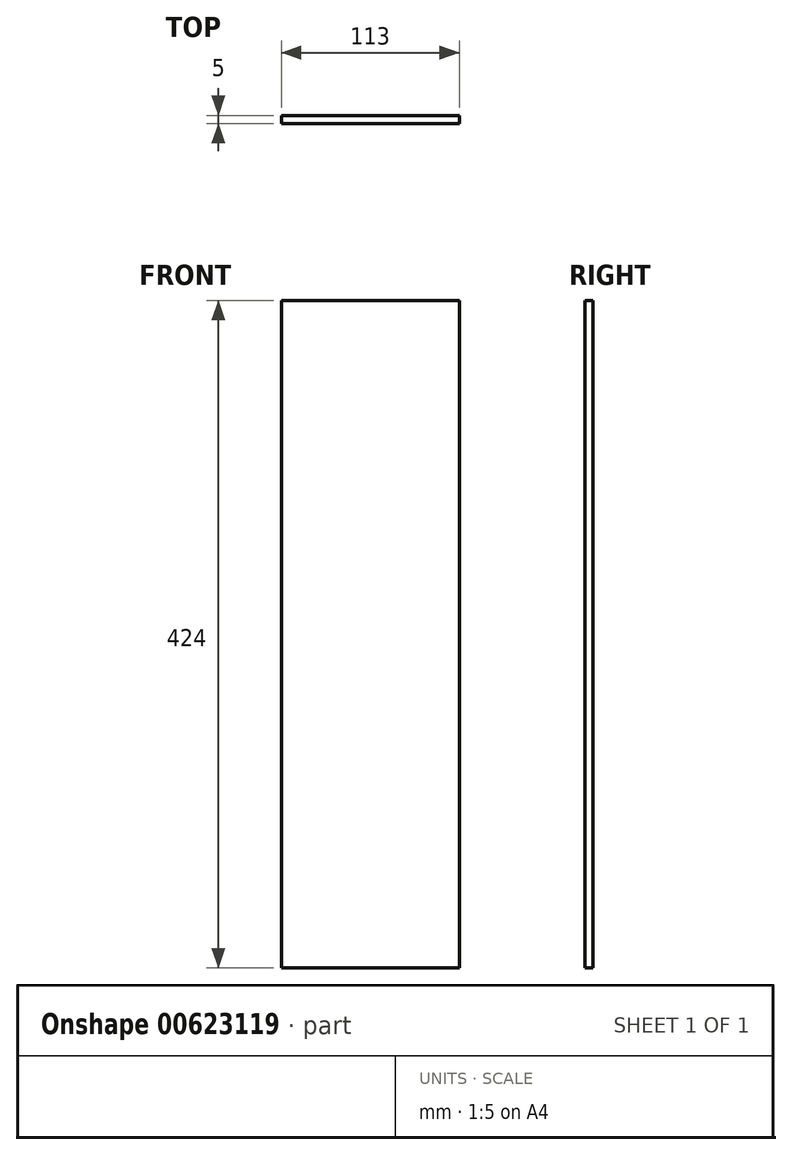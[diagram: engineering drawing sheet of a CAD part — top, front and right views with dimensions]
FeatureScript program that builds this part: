
annotation { "Feature Type Name" : "Feature", "Feature Type Description" : "" }
export const myFeature = defineFeature(function(context is Context, id is Id, definition is map)
    precondition{}
    {
        {
            var Q0;
            Q0=qCreatedBy(makeId("Front.planeOp"),FACE);
            var sketch = newSketch(context, id + "F0", { "sketchPlane" : qUnion([Q0])});
            skLineSegment(sketch, "E0.bottom", {"start": v(0, 0) * mm, "end": v(113, 0) * mm});
            skLineSegment(sketch, "E0.top", {"start": v(0, 424) * mm, "end": v(113, 424) * mm});
            skLineSegment(sketch, "E0.left", {"start": v(0, 0) * mm, "end": v(0, 424) * mm});
            skLineSegment(sketch, "E0.right", {"start": v(113, 0) * mm, "end": v(113, 424) * mm});
            skSolve(sketch);
        }
        {
            var Q0;
            Q0 = qSketchRegion(id + "F0", true);
            extrude(context, id + "F1", {"entities" : qUnion([Q0]), "depth" : 5 * mm, "offsetDistance" : 25 * mm});
        }
    });
